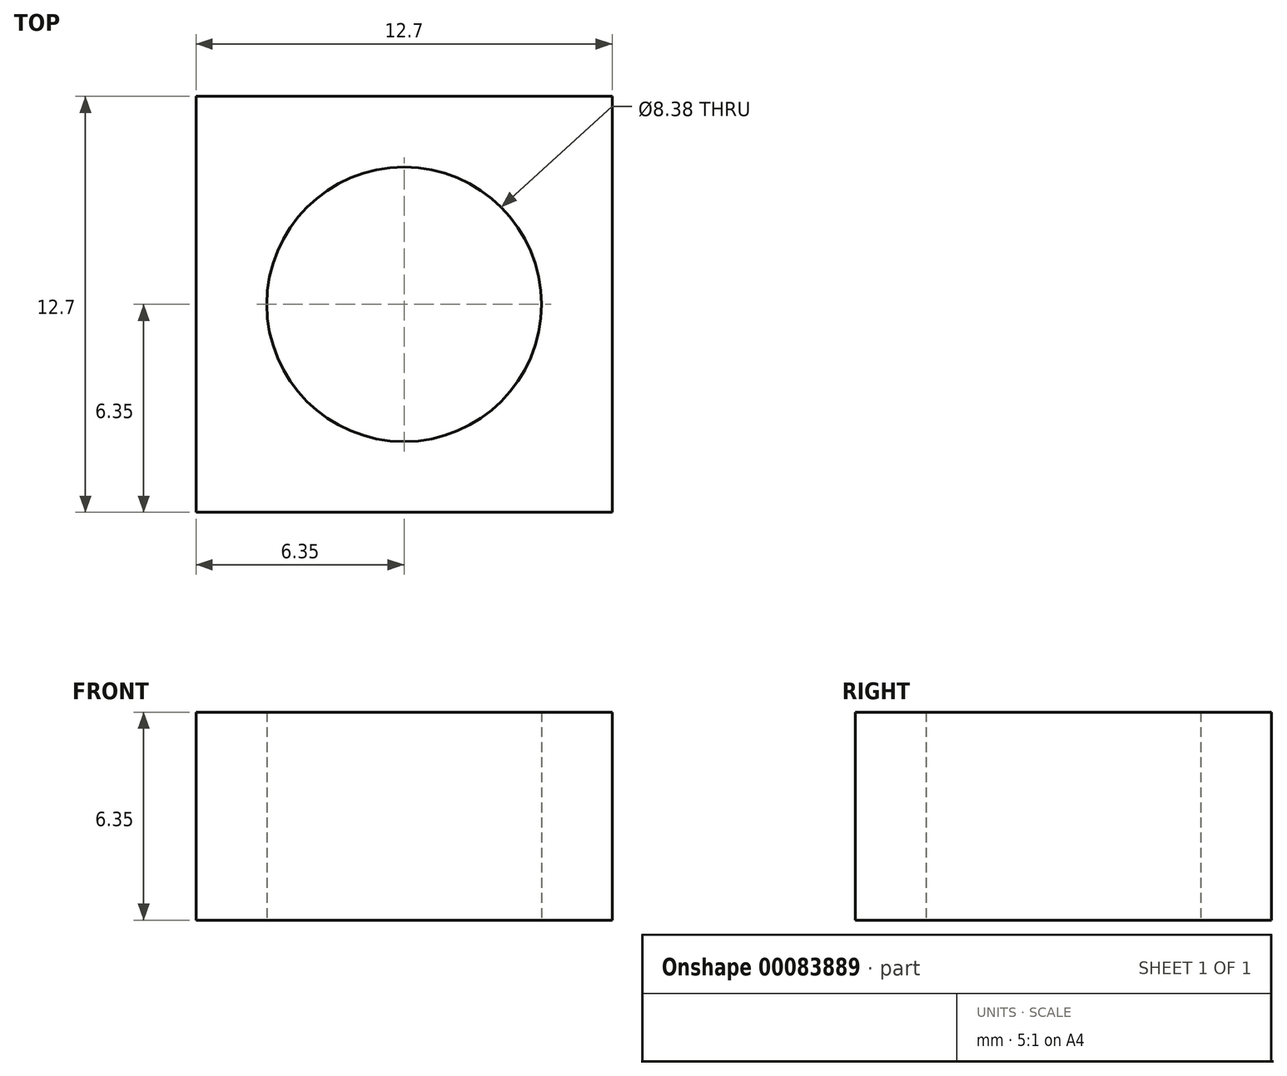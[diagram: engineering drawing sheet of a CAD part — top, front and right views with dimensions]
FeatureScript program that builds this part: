
annotation { "Feature Type Name" : "Feature", "Feature Type Description" : "" }
export const myFeature = defineFeature(function(context is Context, id is Id, definition is map)
    precondition{}
    {
        {
            var Q0;
            Q0=qCreatedBy(makeId("Top.planeOp"),FACE);
            var sketch = newSketch(context, id + "F0", { "sketchPlane" : qUnion([Q0])});
            skLineSegment(sketch, "E0.bottom", {"start": v(6.35, -6.35) * mm, "end": v(-6.35, -6.35) * mm});
            skLineSegment(sketch, "E0.top", {"start": v(6.35, 6.35) * mm, "end": v(-6.35, 6.35) * mm});
            skLineSegment(sketch, "E0.left", {"start": v(6.35, -6.35) * mm, "end": v(6.35, 6.35) * mm});
            skLineSegment(sketch, "E0.right", {"start": v(-6.35, -6.35) * mm, "end": v(-6.35, 6.35) * mm});
            skPoint(sketch, "E0.middle", {"position": v(0, 0) * mm});
            skCircle(sketch, "E1", {"center": v(0, 0) * mm, "radius": 4.2 * mm});
            skSolve(sketch);
        }
        {
            var Q0;
            Q0 = qSketchRegion(id + "F0", true);
            extrude(context, id + "F1", {"entities" : qUnion([Q0]), "depth" : 6.35 * mm});
        }
    });
